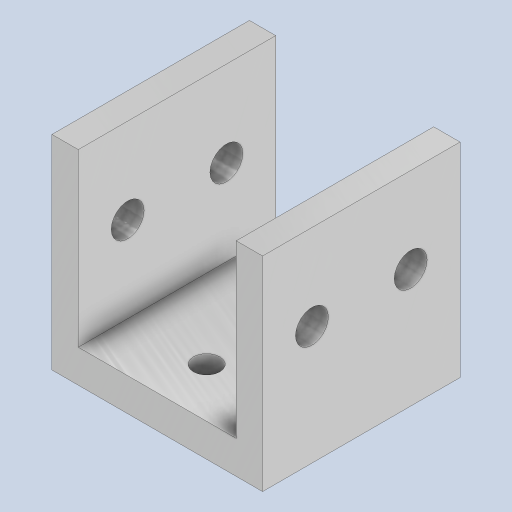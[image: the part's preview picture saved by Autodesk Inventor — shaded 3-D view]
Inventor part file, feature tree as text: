
AUTODESK INVENTOR PART (.ipt)
format: ipt  version: 2023 (Build 270158000, 158)  size: 182,272 bytes
history: native  units: mm
features: sketch x3, extrude x2, hole x2
ambient origin geometry x8: Origin, YZ Plane, XZ Plane, XY Plane, X Axis, Y Axis, Z Axis, Center Point
bodies: Body1 (feature_tree)
feature tree (7):
  extrude  "Extrusion1"  Depth=30.0mm
  extrude  "Extrusion2"  Depth=26.0mm TaperAngle=0.0deg
  hole  "Hole2"  [1 undecoded]
  hole  "Furo3"  [1 undecoded]
  sketch  "Esboço1"  dims[d0=32.0mm d1=30.0mm]
  sketch  "Sketch4"  dims[d24=5.0mm d25=0.0mm d28=26.0mm d29=0.0mm]
  sketch  "Sketch5"  dims[d30=7.5mm d31=7.5mm d32=13.0mm d33=13.0mm d34=5.0mm d35=6.0mm d36=4.0mm d37=2.0mm d38=90.0deg d39=5.0mm d40=20.594885mm d43=15.0mm d45=24.0mm d48=30.0mm d50=4.0mm d51=6.0mm d52=7.0mm d53=3.0mm d54=90.0deg d55=5.0mm d56=20.594885mm d57=12.0mm d58=7.5mm d59=24.0mm d60=0.872665mm]
note: 2 required parameter values undecoded (feature->parameter linkage not recoverable at this tier; creation-order binding heuristic only, values carry confidence <= 0.55)
